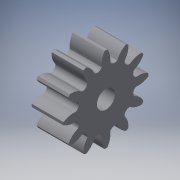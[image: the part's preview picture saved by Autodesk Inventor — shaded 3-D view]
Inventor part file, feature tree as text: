
AUTODESK INVENTOR PART (.ipt)
format: ipt  version: 2016 (Build 200138000, 138)  size: 274,944 bytes
history: native  units: in
note: dims shown in document units (in); Inventor stores cm internally (conversion verified against a paired STEP export)
features: extrude x3, sketch x3, plane x1
ambient origin geometry x8: Origin, YZ Plane, XZ Plane, XY Plane, X Axis, Y Axis, Z Axis, Center Point
bodies: Solid1 (feature_tree)
feature tree (7):
  plane  "Work Plane2"
  extrude  "Extrusion19"  Depth=0.2255in TaperAngle=0.0deg
  extrude  "Extrusion20"  Depth=100.0in TaperAngle=0.0deg
  extrude  "Extrusion21"  Depth=4.7244in TaperAngle=360.0deg
  sketch  "Sketch6"  dims[d92=4.7244in d94=360.0deg d102=0.2255in d103=0.0in]
  sketch  "Sketch7"  dims[d104=0.128in d105=100.0in d106=0.0in]
  sketch  "Sketch8"  dims[d107=0.4in d108=4.7244in d110=360.0deg d112=100.0in d113=0.0in]
